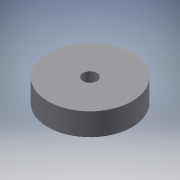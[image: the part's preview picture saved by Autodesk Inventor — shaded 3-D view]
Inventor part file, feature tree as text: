
AUTODESK INVENTOR PART (.ipt)
format: ipt  version: 2018 (Build 220112000, 112)  size: 94,720 bytes
history: native  units: mm
features: extrude x1, sketch x1
ambient origin geometry x8: Origin, YZ Plane, XZ Plane, XY Plane, X Axis, Y Axis, Z Axis, Center Point
bodies: Solid1 (feature_tree)
feature tree (2):
  extrude  "Extrusion1"  Depth=40.0mm
  sketch  "Sketch1"  dims[d0=150.0mm d1=25.0mm d2=40.0mm d3=0.0mm]
